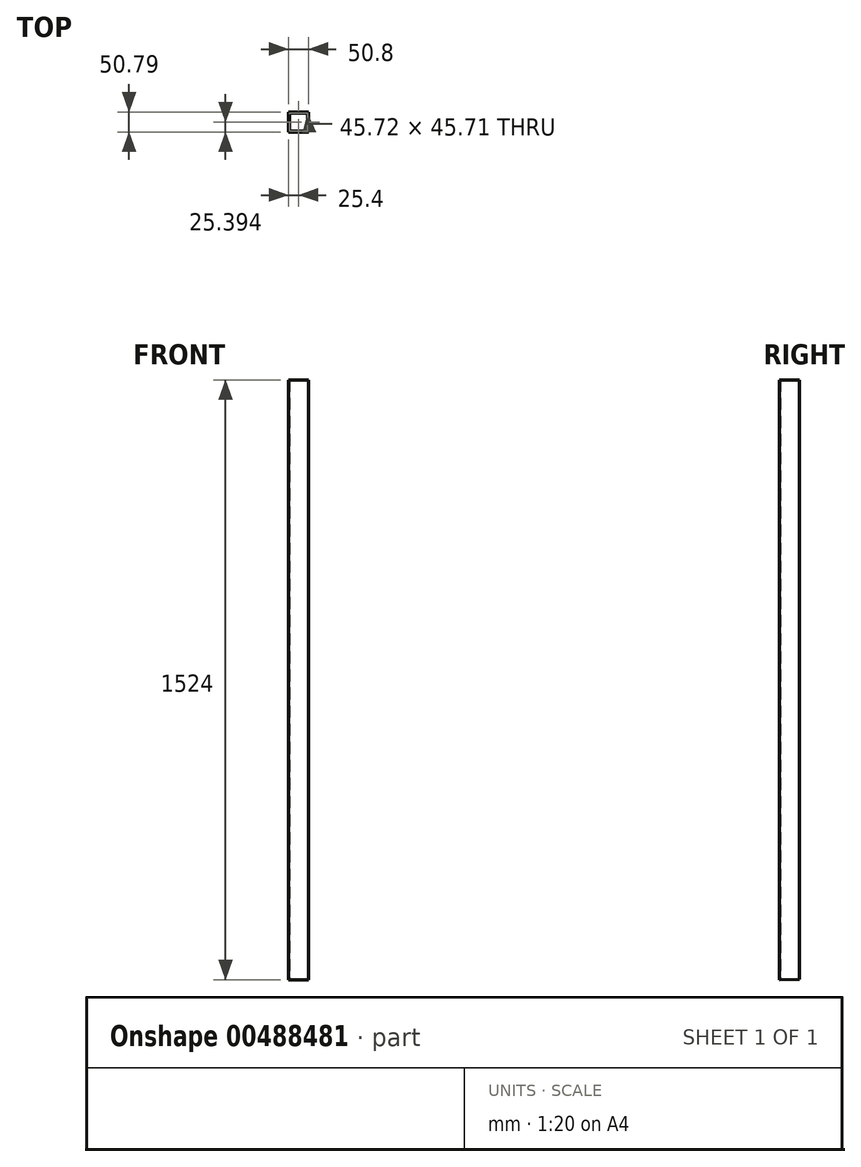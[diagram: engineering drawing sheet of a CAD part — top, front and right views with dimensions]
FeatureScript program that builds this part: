
annotation { "Feature Type Name" : "Feature", "Feature Type Description" : "" }
export const myFeature = defineFeature(function(context is Context, id is Id, definition is map)
    precondition{}
    {
        {
            var Q0;
            Q0=qCreatedBy(makeId("Right.planeOp"),FACE);
            var sketch = newSketch(context, id + "F0", { "sketchPlane" : qUnion([Q0])});
            skLineSegment(sketch, "E0", {"start": v(50.79, 719.81) * mm, "end": v(50.79, -803.08) * mm});
            skLineSegment(sketch, "E1", {"start": v(50.79, 719.81) * mm, "end": v(0, 719.81) * mm});
            skLineSegment(sketch, "E2", {"start": v(0, 719.81) * mm, "end": v(0, -804.19) * mm});
            skLineSegment(sketch, "E3", {"start": v(0, -804.19) * mm, "end": v(50.79, -803.08) * mm});
            skSolve(sketch);
        }
        {
            var Q0;
            Q0=makeQuery(id+"F0.imprint","IMPRINT",FACE,{"disambiguationData":[TD([[makeQuery(id+"F0.imprint","IMPRINT",EDGE,{"derivedFrom":sQuery(id+"F0.wireOp",EDGE,"E0")}),-1.0]])]});
            extrude(context, id + "F1", {"entities" : qUnion([Q0]), "depth" : 50.8 * mm, "symmetric" : true});
        }
        {
            var Q0;
            Q0=makeQuery(id+"F1.opExtrude","SWEPT_FACE",FACE,{"disambiguationData":[OSD([sQuery(id+"F0.wireOp",EDGE,"E3")])]});
            var Q1;
            Q1=makeQuery(id+"F1.opExtrude","SWEPT_FACE",FACE,{"disambiguationData":[OSD([sQuery(id+"F0.wireOp",EDGE,"E1")])]});
            shell(context, id + "F2", {"entities" : qUnion([Q0, Q1]), "thickness" : 2.54 * mm});
        }
    });
